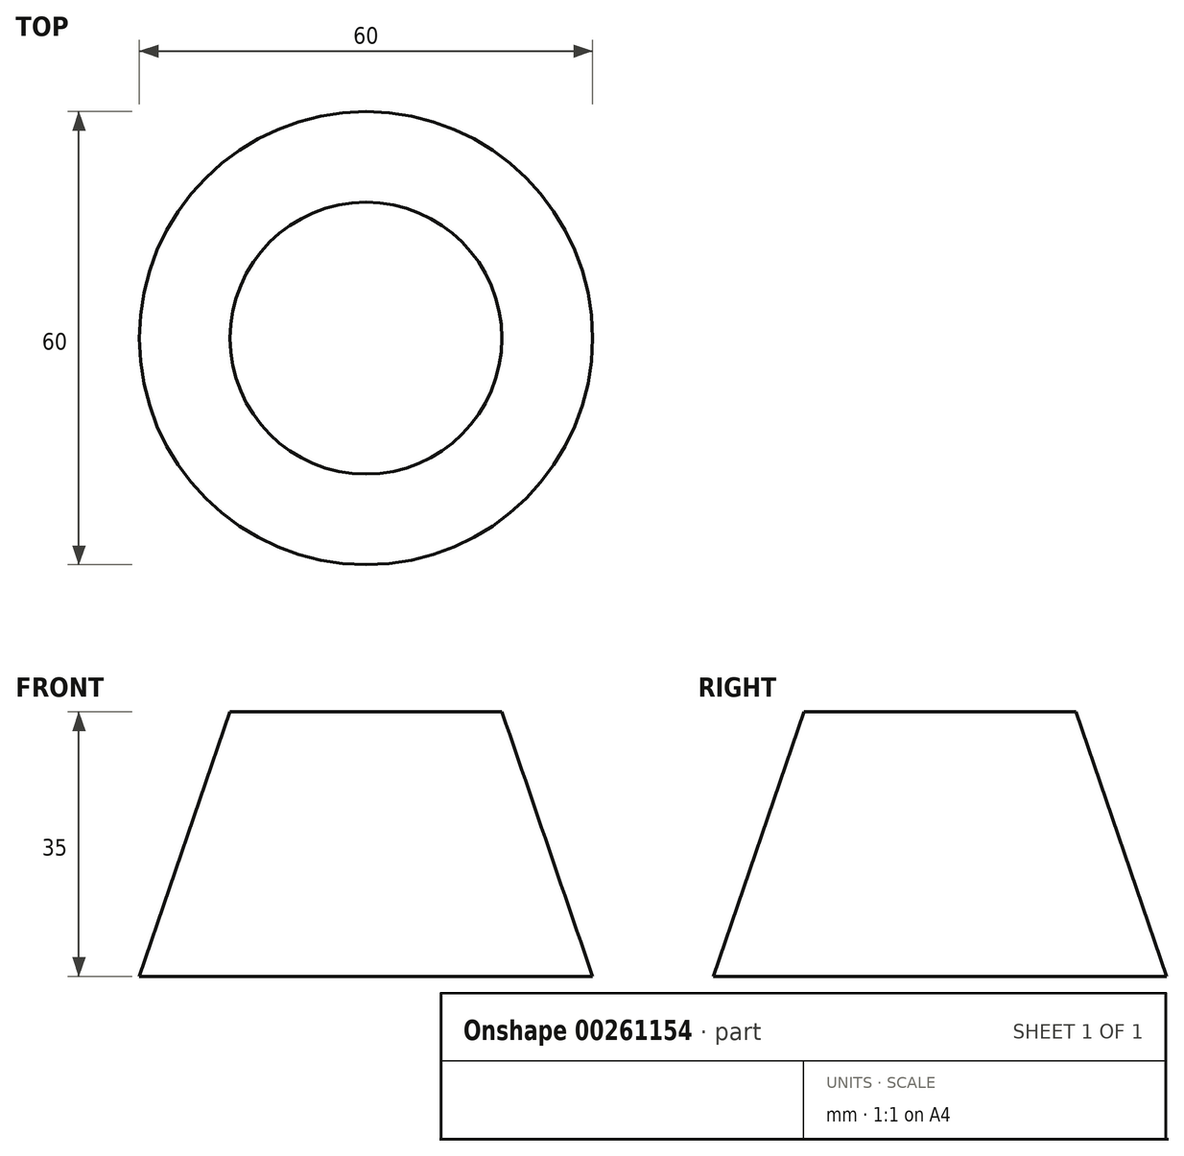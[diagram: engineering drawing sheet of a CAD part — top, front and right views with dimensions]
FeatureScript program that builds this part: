
annotation { "Feature Type Name" : "Feature", "Feature Type Description" : "" }
export const myFeature = defineFeature(function(context is Context, id is Id, definition is map)
    precondition{}
    {
        {
            var Q0;
            Q0=qCreatedBy(makeId("Front.planeOp"),FACE);
            var sketch = newSketch(context, id + "F0", { "sketchPlane" : qUnion([Q0])});
            skLineSegment(sketch, "E0", {"start": v(0, 0) * mm, "end": v(0, 35) * mm});
            skLineSegment(sketch, "E1", {"start": v(0, 35) * mm, "end": v(18, 35) * mm});
            skLineSegment(sketch, "E2", {"start": v(18, 35) * mm, "end": v(30, 0) * mm});
            skLineSegment(sketch, "E3", {"start": v(30, 0) * mm, "end": v(0, 0) * mm});
            skLineSegment(sketch, "E4", {"start": v(0, 58.83) * mm, "end": v(0, -53.25) * mm, "construction": true});
            skSolve(sketch);
        }
        {
            var Q0;
            Q0=makeQuery(id+"F0.imprint","IMPRINT",FACE,{"disambiguationData":[TD([[makeQuery(id+"F0.imprint","IMPRINT",EDGE,{"derivedFrom":sQuery(id+"F0.wireOp",EDGE,"E0")}),-1.0]])]});
            var Q1;
            Q1=sQuery(id+"F0.wireOp",EDGE,"E4");
            revolve(context, id + "F1", {"entities" : qUnion([Q0]), "axis" : qUnion([Q1]), "revolveType" : RevolveType.FULL});
        }
    });
